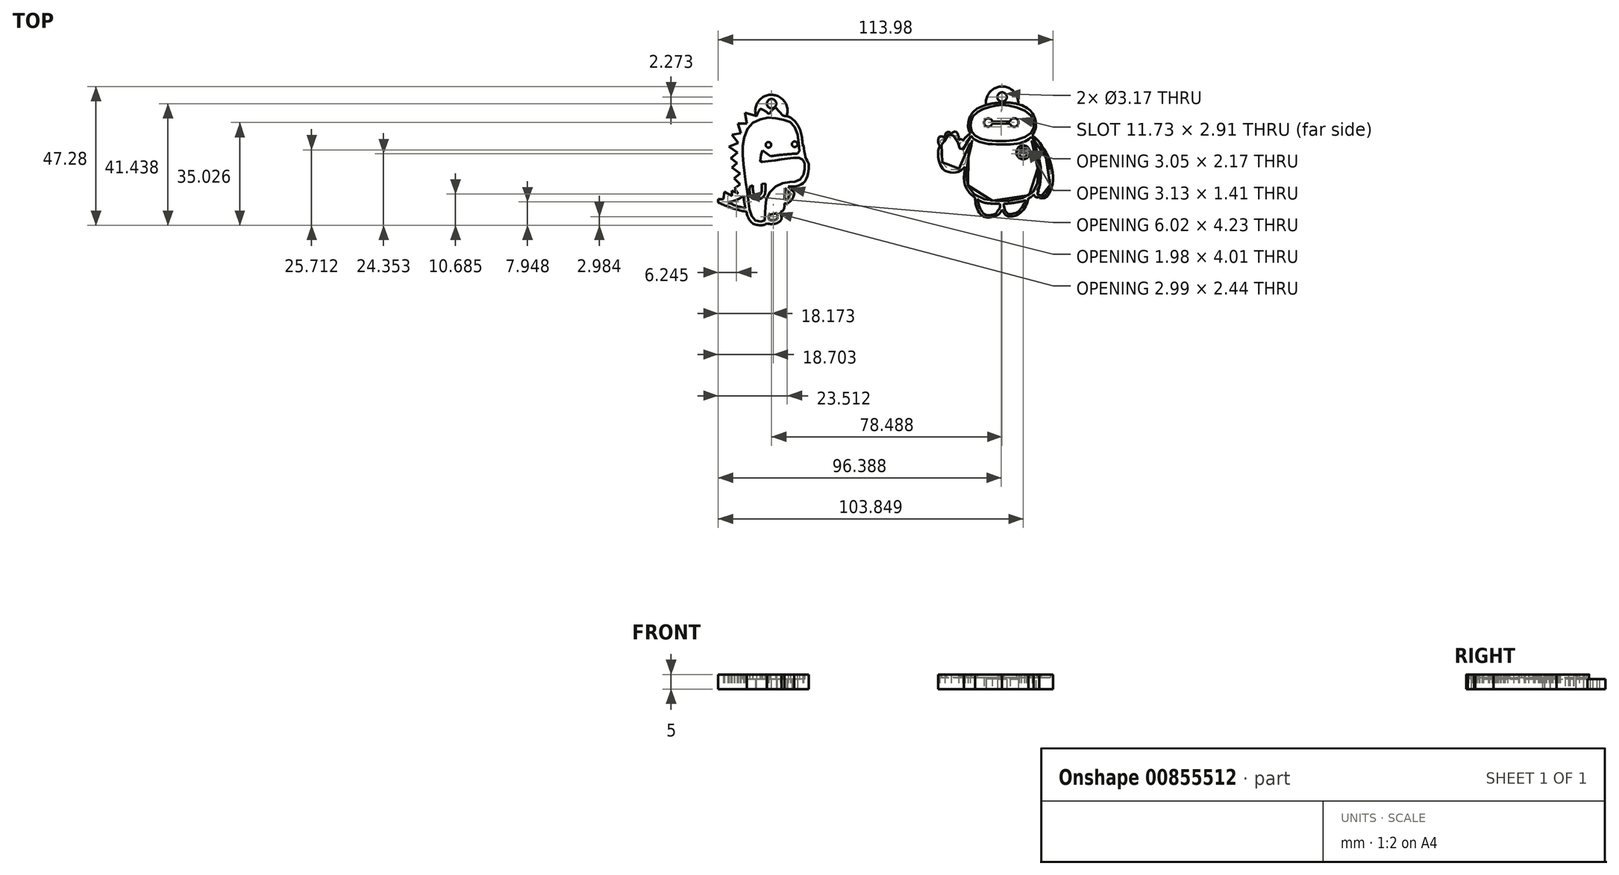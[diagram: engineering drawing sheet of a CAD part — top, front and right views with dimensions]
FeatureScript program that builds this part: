
annotation { "Feature Type Name" : "Feature", "Feature Type Description" : "" }
export const myFeature = defineFeature(function(context is Context, id is Id, definition is map)
    precondition{}
    {
        {
            var Q0;
            Q0=qCreatedBy(makeId("Top.planeOp"),FACE);
            var sketch = newSketch(context, id + "F0", { "sketchPlane" : qUnion([Q0])});
            skFitSpline(sketch, "E0", {"points": [v(-13.55, 2.38) * mm, v(-14.14, 6.7) * mm, v(-15.54, 10.04) * mm, v(-18.18, 12.36) * mm, v(-20.34, 12.79) * mm], "startDerivative": vector(-1.53, 15.7) * mm, "endDerivative": vector(-10.5, 0.69) * mm});
            skLineSegment(sketch, "E1", {"start": v(-20.34, 12.79) * mm, "end": v(-22.82, 15.65) * mm});
            skFitSpline(sketch, "E2", {"points": [v(-22.82, 15.65) * mm, v(-24.28, 14.43) * mm, v(-25.04, 13.33) * mm], "startDerivative": vector(-2.96, -2.18) * mm, "endDerivative": vector(-1.42, -2.46) * mm});
            skFitSpline(sketch, "E3", {"points": [v(-25.04, 13.33) * mm, v(-26.95, 14.76) * mm, v(-28.08, 15.13) * mm], "startDerivative": vector(-3.43, 2.89) * mm, "endDerivative": vector(-2.63, 0.6) * mm});
            skFitSpline(sketch, "E4", {"points": [v(-28.08, 15.13) * mm, v(-28.76, 14) * mm, v(-29.3, 12.68) * mm], "startDerivative": vector(-1.45, -2.24) * mm, "endDerivative": vector(-0.98, -2.66) * mm});
            skFitSpline(sketch, "E5", {"points": [v(-29.3, 12.68) * mm, v(-33.32, 13.87) * mm], "startDerivative": vector(-4.02, 1.19) * mm, "endDerivative": vector(-4.02, 1.19) * mm});
            skLineSegment(sketch, "E6", {"start": v(-33.32, 13.87) * mm, "end": v(-32.7, 10.17) * mm});
            skLineSegment(sketch, "E7", {"start": v(-32.7, 10.17) * mm, "end": v(-35.72, 10.17) * mm});
            skLineSegment(sketch, "E8", {"start": v(-35.72, 10.17) * mm, "end": v(-34.67, 6.85) * mm});
            skLineSegment(sketch, "E9", {"start": v(-34.67, 6.85) * mm, "end": v(-37.66, 6.31) * mm});
            skLineSegment(sketch, "E10", {"start": v(-37.66, 6.31) * mm, "end": v(-35.58, 3.6) * mm});
            skLineSegment(sketch, "E11", {"start": v(-35.58, 3.6) * mm, "end": v(-38.74, 2.24) * mm});
            skLineSegment(sketch, "E12", {"start": v(-38.74, 2.24) * mm, "end": v(-35.82, 0.22) * mm});
            skLineSegment(sketch, "E13", {"start": v(-35.82, 0.22) * mm, "end": v(-38.06, -1.67) * mm});
            skLineSegment(sketch, "E14", {"start": v(-38.06, -1.67) * mm, "end": v(-35.88, -3.34) * mm});
            skLineSegment(sketch, "E15", {"start": v(-35.88, -3.34) * mm, "end": v(-37.71, -4.85) * mm});
            skLineSegment(sketch, "E16", {"start": v(-37.71, -4.85) * mm, "end": v(-34.93, -6.82) * mm});
            skLineSegment(sketch, "E17", {"start": v(-34.93, -6.82) * mm, "end": v(-36.98, -8.5) * mm});
            skLineSegment(sketch, "E18", {"start": v(-36.98, -8.5) * mm, "end": v(-34.93, -10.49) * mm});
            skLineSegment(sketch, "E19", {"start": v(-34.93, -10.49) * mm, "end": v(-36.85, -11.95) * mm});
            skLineSegment(sketch, "E20", {"start": v(-36.85, -11.95) * mm, "end": v(-35.53, -13.68) * mm});
            skLineSegment(sketch, "E21", {"start": v(-35.53, -13.68) * mm, "end": v(-37.66, -12.76) * mm});
            skLineSegment(sketch, "E22", {"start": v(-37.66, -12.76) * mm, "end": v(-37.66, -14.54) * mm});
            skLineSegment(sketch, "E23", {"start": v(-37.66, -14.54) * mm, "end": v(-40.22, -13.08) * mm});
            skLineSegment(sketch, "E24", {"start": v(-40.22, -13.08) * mm, "end": v(-40.68, -15.61) * mm});
            skLineSegment(sketch, "E25", {"start": v(-40.68, -15.61) * mm, "end": v(-42.38, -15.61) * mm});
            skLineSegment(sketch, "E26", {"start": v(-42.38, -15.61) * mm, "end": v(-42.38, -16.75) * mm});
            skFitSpline(sketch, "E27", {"points": [v(-42.38, -16.75) * mm, v(-38.06, -18.5) * mm, v(-32.7, -19.98) * mm], "startDerivative": vector(8.74, -3.87) * mm, "endDerivative": vector(10.6, -2.62) * mm});
            skFitSpline(sketch, "E28", {"points": [v(-33.13, -18.69) * mm, v(-33.59, -16.23) * mm, v(-33.77, -14.45) * mm], "startDerivative": vector(-0.96, 4.7) * mm, "endDerivative": vector(-0.31, 3.73) * mm});
            skFitSpline(sketch, "E29", {"points": [v(-33.77, -14.45) * mm, v(-35.9, -15.78) * mm, v(-39.14, -16.75) * mm], "startDerivative": vector(-4.28, -3.1) * mm, "endDerivative": vector(-6.4, -1.53) * mm});
            skFitSpline(sketch, "E30", {"points": [v(-39.14, -16.75) * mm, v(-36.74, -17.7) * mm, v(-34.53, -18.4) * mm, v(-33.13, -18.69) * mm], "startDerivative": vector(6.42, -2.62) * mm, "endDerivative": vector(4.8, -0.89) * mm});
            skCircle(sketch, "E31", {"center": v(-25.27, 2.88) * mm, "radius": 0.94 * mm});
            skCircle(sketch, "E32", {"center": v(-16.34, 3.1) * mm, "radius": 0.94 * mm});
            skFitSpline(sketch, "E33", {"points": [v(-32.7, -19.98) * mm, v(-32.33, -21.5) * mm, v(-30.9, -23.65) * mm, v(-29.2, -24.4) * mm, v(-26.91, -24.42) * mm, v(-25.82, -23.82) * mm], "startDerivative": vector(1.1, -7.8) * mm, "endDerivative": vector(5.74, 4.5) * mm});
            skFitSpline(sketch, "E34", {"points": [v(-25.82, -23.82) * mm, v(-24.76, -24.07) * mm, v(-22.61, -23.82) * mm, v(-20.95, -22.56) * mm, v(-21.24, -19.98) * mm], "startDerivative": vector(5.1, -1.72) * mm, "endDerivative": vector(-2.9, 9.83) * mm});
            skFitSpline(sketch, "E35", {"points": [v(-21.24, -19.98) * mm, v(-20.27, -19.45) * mm, v(-19.86, -18.2) * mm, v(-19.86, -17.01) * mm], "startDerivative": vector(3.4, 1.17) * mm, "endDerivative": vector(-0.19, 3.45) * mm});
            skFitSpline(sketch, "E36", {"points": [v(-19.86, -17.01) * mm, v(-18.73, -17.01) * mm, v(-17.07, -15.35) * mm, v(-16.58, -13.4) * mm, v(-17.29, -12.59) * mm, v(-18.5, -11.3) * mm], "startDerivative": vector(6.54, -1.35) * mm, "endDerivative": vector(-5.93, 6.76) * mm});
            skFitSpline(sketch, "E37", {"points": [v(-18.5, -11.3) * mm, v(-16.3, -11.3) * mm, v(-13.28, -10) * mm, v(-11.7, -6.53) * mm, v(-11.64, -3.38) * mm, v(-12.48, -1.75) * mm, v(-13.28, 2.78) * mm], "startDerivative": vector(14.75, -1.2) * mm, "endDerivative": vector(-2.71, 25.65) * mm});
            skFitSpline(sketch, "E38", {"points": [v(-13.28, 2.78) * mm, v(-13.55, 2.38) * mm], "startDerivative": vector(-0.26, -0.4) * mm, "endDerivative": vector(-0.26, -0.4) * mm});
            skFitSpline(sketch, "E39", {"points": [v(-31.58, -11.3) * mm, v(-30.59, -10.94) * mm], "startDerivative": vector(1, 0.36) * mm, "endDerivative": vector(1, 0.36) * mm});
            skFitSpline(sketch, "E40", {"points": [v(-31.58, -11.3) * mm, v(-31.71, -12.51) * mm, v(-31.34, -14.6) * mm, v(-30.3, -15.56) * mm, v(-28.36, -15.62) * mm, v(-26.77, -14.5) * mm, v(-26.37, -13.31) * mm, v(-26.32, -10.27) * mm], "startDerivative": vector(-1.66, -9.24) * mm, "endDerivative": vector(-0.24, 18.42) * mm});
            skFitSpline(sketch, "E41", {"points": [v(-30.59, -10.94) * mm, v(-30.59, -12.35) * mm, v(-30.19, -13.84) * mm, v(-29.28, -14.6) * mm, v(-28.04, -13.99) * mm, v(-27.54, -12.82) * mm, v(-27.56, -10.38) * mm], "startDerivative": vector(-0.38, -8.61) * mm, "endDerivative": vector(-0.72, 12.58) * mm});
            skFitSpline(sketch, "E42", {"points": [v(-27.56, -10.38) * mm, v(-26.32, -10.27) * mm], "startDerivative": vector(1.23, 0.11) * mm, "endDerivative": vector(1.23, 0.11) * mm});
            skFitSpline(sketch, "E43", {"points": [v(-25.17, -20.9) * mm, v(-23.34, -20.61) * mm, v(-22.45, -20.31) * mm], "startDerivative": vector(3.43, 0.45) * mm, "endDerivative": vector(1.94, 0.76) * mm});
            skFitSpline(sketch, "E44", {"points": [v(-25.17, -20.9) * mm, v(-25.17, -22.49) * mm], "startDerivative": vector(0, -1.58) * mm, "endDerivative": vector(0, -1.58) * mm});
            skFitSpline(sketch, "E45", {"points": [v(-25.17, -22.49) * mm, v(-24.72, -22.7) * mm, v(-23.5, -22.73) * mm, v(-22.52, -22.49) * mm, v(-22.2, -22.03) * mm, v(-22.22, -21.27) * mm, v(-22.45, -20.31) * mm], "startDerivative": vector(2.97, -1.91) * mm, "endDerivative": vector(-1.45, 5.3) * mm});
            skFitSpline(sketch, "E46", {"points": [v(-19.86, -15.84) * mm, v(-19.67, -11.83) * mm], "startDerivative": vector(0.18, 4) * mm, "endDerivative": vector(0.18, 4) * mm});
            skFitSpline(sketch, "E47", {"points": [v(-19.67, -11.83) * mm, v(-18.7, -12.96) * mm, v(-17.9, -13.67) * mm, v(-17.88, -14.04) * mm, v(-18.23, -14.7) * mm, v(-19.04, -15.6) * mm, v(-19.86, -15.84) * mm], "startDerivative": vector(4.22, -5.71) * mm, "endDerivative": vector(-5.2, -0.73) * mm});
            skFitSpline(sketch, "E48", {"points": [v(-24.55, -1.02) * mm, v(-20.5, -0.46) * mm, v(-17.07, -0.18) * mm, v(-15.46, -0.14) * mm], "startDerivative": vector(10.3, 1.59) * mm, "endDerivative": vector(5.92, 0.1) * mm});
            skFitSpline(sketch, "E49", {"points": [v(-15.46, -0.14) * mm, v(-14.75, 0.77) * mm], "startDerivative": vector(0.7, 0.9) * mm, "endDerivative": vector(0.7, 0.9) * mm});
            skFitSpline(sketch, "E50", {"points": [v(-14.75, 0.77) * mm, v(-15.12, 5.03) * mm, v(-16.34, 8.98) * mm, v(-18.04, 10.7) * mm, v(-21.24, 11.68) * mm, v(-24.7, 12.15) * mm, v(-28.7, 11.36) * mm, v(-31.76, 9.32) * mm, v(-33.71, 4.9) * mm, v(-34.05, 0.3) * mm, v(-33.62, -5) * mm, v(-33.01, -9.96) * mm, v(-32.29, -14.9) * mm, v(-31.58, -19.67) * mm, v(-30.59, -22.07) * mm, v(-29.04, -23.07) * mm, v(-27.56, -23.18) * mm, v(-26.52, -22.91) * mm], "startDerivative": vector(-2.74, 64.84) * mm, "endDerivative": vector(30.23, 10.18) * mm});
            skFitSpline(sketch, "E51", {"points": [v(-26.52, -22.91) * mm, v(-26.32, -18.87) * mm, v(-25.82, -15) * mm, v(-22.28, -10.94) * mm, v(-18.1, -9.76) * mm, v(-15.75, -9.6) * mm, v(-13.55, -7.8) * mm, v(-13, -5.47) * mm, v(-12.98, -3.04) * mm, v(-13.85, -2.02) * mm, v(-15.25, -1.5) * mm, v(-17.95, -1.64) * mm, v(-20.91, -2.06) * mm, v(-24.37, -2.54) * mm, v(-27.56, -3) * mm, v(-27.98, -3) * mm, v(-27.93, -0.91) * mm, v(-27.25, 0.97) * mm], "startDerivative": vector(3.63, 55.97) * mm, "endDerivative": vector(15.3, 32.1) * mm});
            skFitSpline(sketch, "E52", {"points": [v(-27.25, 0.97) * mm, v(-24.55, -1.02) * mm], "startDerivative": vector(2.7, -2) * mm, "endDerivative": vector(2.7, -2) * mm});
            skArc(sketch, "E53", {"start": v(-19.08, 12.65) * mm, "mid": v(-24.23, 19.93) * mm, "end": v(-29.51, 12.74) * mm});
            skCircle(sketch, "E54", {"center": v(-24.2, 16.92) * mm, "radius": 1.59 * mm});
            skFitSpline(sketch, "E55", {"points": [v(52.83, 17.2) * mm, v(57.19, 17.2) * mm, v(61.36, 16.2) * mm, v(64.4, 13.95) * mm, v(65.79, 10.46) * mm, v(65.6, 7.99) * mm, v(64.57, 6.22) * mm], "startDerivative": vector(23.07, 1.03) * mm, "endDerivative": vector(-9.18, -12.95) * mm});
            skFitSpline(sketch, "E56", {"points": [v(52.83, 17.2) * mm, v(49.94, 16.77) * mm, v(46.6, 15.62) * mm, v(44.62, 14.27) * mm, v(43.27, 12.22) * mm, v(42.75, 10.3) * mm, v(42.85, 8.15) * mm, v(43.46, 6.73) * mm], "startDerivative": vector(-17.72, -1.72) * mm, "endDerivative": vector(6.22, -11.36) * mm});
            skFitSpline(sketch, "E57", {"points": [v(43.46, 6.73) * mm, v(42.45, 5.98) * mm, v(41.47, 4.99) * mm, v(40.94, 4.32) * mm], "startDerivative": vector(-2.92, -1.98) * mm, "endDerivative": vector(-1.67, -2.23) * mm});
            skFitSpline(sketch, "E58", {"points": [v(40.94, 4.32) * mm, v(40.6, 4.68) * mm, v(40.07, 4.83) * mm, v(39.5, 4.57) * mm], "startDerivative": vector(-0.93, 1.29) * mm, "endDerivative": vector(-1.6, -1) * mm});
            skFitSpline(sketch, "E59", {"points": [v(39.5, 4.57) * mm, v(39.5, 5.44) * mm, v(39.2, 6.45) * mm, v(38.7, 7.3) * mm, v(38, 7.4) * mm, v(37.31, 6.96) * mm, v(37.01, 6.2) * mm], "startDerivative": vector(0.38, 5.14) * mm, "endDerivative": vector(-1.3, -5.03) * mm});
            skFitSpline(sketch, "E60", {"points": [v(37.01, 6.2) * mm, v(36.58, 7.04) * mm, v(36, 7.3) * mm, v(35.47, 7.14) * mm, v(35.09, 6.73) * mm, v(34.86, 6.2) * mm, v(34.8, 5.52) * mm, v(34.85, 4.86) * mm], "startDerivative": vector(-2.07, 5.55) * mm, "endDerivative": vector(0.47, -4.5) * mm});
            skFitSpline(sketch, "E61", {"points": [v(34.85, 4.86) * mm, v(34.36, 5.44) * mm, v(33.79, 5.77) * mm, v(33.02, 5.63) * mm, v(32.63, 5.09) * mm, v(32.52, 3.64) * mm, v(32.82, 2.94) * mm, v(33.06, 2.47) * mm], "startDerivative": vector(-3.3, 4.35) * mm, "endDerivative": vector(1.91, -3.92) * mm});
            skFitSpline(sketch, "E62", {"points": [v(33.06, 2.47) * mm, v(32.7, 1.48) * mm, v(32.49, -0.2) * mm, v(32.6, -1.84) * mm, v(33.06, -3.5) * mm, v(34, -5.18) * mm, v(35.13, -6.03) * mm, v(38.16, -6.57) * mm, v(40.09, -5.87) * mm, v(41.66, -4.54) * mm], "startDerivative": vector(-4.76, -10.76) * mm, "endDerivative": vector(12.96, 12.08) * mm});
            skFitSpline(sketch, "E63", {"points": [v(41.66, -4.54) * mm, v(41.47, -6.27) * mm, v(41.36, -9.32) * mm, v(41.98, -11.6) * mm, v(43.46, -13.74) * mm, v(45.06, -15.14) * mm], "startDerivative": vector(-1.09, -9.17) * mm, "endDerivative": vector(8.58, -6.65) * mm});
            skFitSpline(sketch, "E64", {"points": [v(45.06, -15.14) * mm, v(45.23, -16.76) * mm, v(45.82, -18.9) * mm, v(47.05, -20.9) * mm, v(48.74, -21.78) * mm, v(50.98, -21.71) * mm, v(52.94, -20.96) * mm, v(53.6, -20.27) * mm, v(54.22, -19.25) * mm], "startDerivative": vector(0.88, -13.14) * mm, "endDerivative": vector(6.2, 10.64) * mm});
            skFitSpline(sketch, "E65", {"points": [v(54.22, -19.25) * mm, v(54.8, -20.2) * mm, v(56.02, -21.36) * mm, v(57.66, -21.47) * mm, v(59.64, -20.9) * mm, v(61.68, -19) * mm, v(62.87, -16.73) * mm, v(63.32, -15.36) * mm], "startDerivative": vector(4.53, -8.12) * mm, "endDerivative": vector(3.02, 10.17) * mm});
            skFitSpline(sketch, "E66", {"points": [v(63.32, -15.36) * mm, v(64.7, -14.45) * mm, v(65.06, -13.97) * mm], "startDerivative": vector(2.6, 1.53) * mm, "endDerivative": vector(0.75, 1.24) * mm});
            skFitSpline(sketch, "E67", {"points": [v(65.06, -13.97) * mm, v(65.3, -14.38) * mm, v(65.65, -14.8) * mm, v(66.42, -15.03) * mm, v(66.91, -14.8) * mm], "startDerivative": vector(1.04, -1.82) * mm, "endDerivative": vector(1.83, 1.3) * mm});
            skFitSpline(sketch, "E68", {"points": [v(66.91, -14.8) * mm, v(67.03, -15.14) * mm, v(67.96, -15.36) * mm, v(69.37, -14.88) * mm, v(70.68, -12.86) * mm, v(71.46, -10.29) * mm, v(71.55, -7.08) * mm, v(71.02, -4.08) * mm, v(69.81, -0.8) * mm, v(67.82, 2.66) * mm, v(66.44, 4.42) * mm, v(64.92, 5.87) * mm, v(64.57, 6.22) * mm], "startDerivative": vector(0.82, -10.48) * mm, "endDerivative": vector(-6.71, 7.06) * mm});
            skCircle(sketch, "E69", {"center": v(49.56, 10.48) * mm, "radius": 1.42 * mm});
            skCircle(sketch, "E70", {"center": v(58.41, 10.5) * mm, "radius": 1.46 * mm});
            skLineSegment(sketch, "E71", {"start": v(50.95, 10.78) * mm, "end": v(56.98, 10.78) * mm});
            skLineSegment(sketch, "E72", {"start": v(50.96, 10.21) * mm, "end": v(56.98, 10.21) * mm});
            skArc(sketch, "E73", {"start": v(59.76, 16.74) * mm, "mid": v(54.15, 22.75) * mm, "end": v(48.84, 16.48) * mm});
            skCircle(sketch, "E74", {"center": v(54.28, 19.2) * mm, "radius": 1.59 * mm});
            skFitSpline(sketch, "E75", {"points": [v(54.35, 16.46) * mm, v(51.09, 16.02) * mm, v(48.36, 15.3) * mm, v(45.79, 13.88) * mm, v(43.95, 11.92) * mm, v(43.54, 10.12) * mm, v(43.67, 8.08) * mm, v(44.89, 6.21) * mm, v(47.4, 4.9) * mm, v(51.24, 4.29) * mm, v(58.35, 4.46) * mm, v(63.5, 6.38) * mm, v(64.93, 8.6) * mm, v(64.84, 11.3) * mm, v(62.9, 14.05) * mm, v(57.82, 15.98) * mm, v(54.35, 16.46) * mm]});
            skFitSpline(sketch, "E76", {"points": [v(43.7, 6.02) * mm, v(42.39, 4.76) * mm, v(41.32, 3.27) * mm, v(40.77, 2.42) * mm, v(40.88, 1.58) * mm, v(41.2, 0.55) * mm, v(41.2, -0.33) * mm, v(40.79, -0.44) * mm, v(40.3, -0.14) * mm, v(40.2, 0.93) * mm, v(39.8, 1.86) * mm, v(39.74, 2.51) * mm, v(40.31, 3.35) * mm, v(40.5, 3.88) * mm, v(40.06, 4.06) * mm, v(39.78, 4.04) * mm, v(39.28, 3.73) * mm, v(39, 3.83) * mm, v(38.88, 4.82) * mm, v(38.69, 5.93) * mm, v(38.38, 6.57) * mm, v(38.06, 6.57) * mm, v(37.75, 6.02) * mm, v(37.56, 5.05) * mm, v(37.26, 4.82) * mm, v(36.82, 4.78) * mm, v(36.57, 5.07) * mm, v(36.48, 5.9) * mm, v(36.25, 6.35) * mm, v(35.94, 6.46) * mm, v(35.4, 6.04) * mm, v(35.4, 5.18) * mm, v(35.4, 4.29) * mm, v(35.27, 3.92) * mm, v(34.63, 3.62) * mm, v(34.53, 4.2) * mm, v(34.15, 4.69) * mm, v(33.83, 4.9) * mm, v(33.31, 4.6) * mm, v(33.18, 4.32) * mm, v(33.14, 3.77) * mm, v(33.46, 3.14) * mm, v(33.75, 2.5) * mm, v(33.62, 1.75) * mm, v(33.23, 0.15) * mm, v(33.52, -2.05) * mm, v(34.38, -4.07) * mm, v(35.75, -5.35) * mm, v(37.41, -5.67) * mm, v(39.76, -5.16) * mm, v(41.63, -3.5) * mm, v(42.2, -1.3) * mm, v(43.84, 4.46) * mm, v(44.07, 4.42) * mm, v(44.07, 3.98) * mm, v(43.86, 2.97) * mm, v(42.71, -1.7) * mm, v(42.2, -6.41) * mm, v(42.43, -9.85) * mm, v(43.97, -13.22) * mm, v(47.88, -15.5) * mm, v(52.92, -16.18) * mm, v(60.5, -15.44) * mm, v(65.1, -12.77) * mm, v(66.42, -9.2) * mm, v(66.42, -4.45) * mm, v(65.5, 0.03) * mm, v(64.55, 3.31) * mm, v(64.38, 4.4) * mm, v(64.57, 4.38) * mm, v(64.91, 4.1) * mm, v(65.9, 1.65) * mm, v(67.05, -2.28) * mm, v(67.47, -6.1) * mm, v(67.34, -9.64) * mm, v(66.92, -11.4) * mm, v(66.2, -12.73) * mm, v(66.38, -12.7) * mm, v(66.82, -12.8) * mm, v(66.9, -13.17) * mm, v(66.61, -13.43) * mm, v(66.3, -13.83) * mm, v(66.17, -14.25) * mm, v(66.61, -14.27) * mm, v(66.82, -13.97) * mm, v(67.07, -13.72) * mm, v(67.58, -13.7) * mm, v(67.68, -13.9) * mm, v(67.58, -14.3) * mm, v(67.7, -14.54) * mm, v(67.97, -14.6) * mm, v(68.63, -14.58) * mm, v(69.17, -13.97) * mm, v(69.38, -13.74) * mm, v(70.31, -11.77) * mm, v(70.9, -8.7) * mm, v(70.64, -5.58) * mm, v(68.65, -0.3) * mm, v(66.06, 3.75) * mm, v(64.76, 4.97) * mm, v(64.2, 5.53) * mm], "startDerivative": vector(-114.33, -97.1) * mm, "endDerivative": vector(-63.13, 67.13) * mm});
            skFitSpline(sketch, "E77", {"points": [v(43.7, 6.02) * mm, v(44.75, 4.86) * mm, v(47.98, 3.48) * mm, v(54.73, 3) * mm, v(60.03, 3.39) * mm, v(63.06, 4.63) * mm, v(64.2, 5.53) * mm], "startDerivative": vector(7.66, -10.47) * mm, "endDerivative": vector(9.04, 8.09) * mm});
            skFitSpline(sketch, "E78", {"points": [v(45.89, -15.66) * mm, v(47.61, -16.61) * mm, v(51.44, -17.18) * mm, v(53.52, -17.18) * mm], "startDerivative": vector(4.97, -3.6) * mm, "endDerivative": vector(6.14, 0.2) * mm});
            skFitSpline(sketch, "E79", {"points": [v(53.52, -17.18) * mm, v(53.52, -18.37) * mm, v(52.9, -19.47) * mm, v(52.06, -20.52) * mm, v(50.2, -21.04) * mm, v(48.48, -20.88) * mm, v(47.45, -19.8) * mm, v(46.5, -17.99) * mm, v(45.89, -15.66) * mm], "startDerivative": vector(1.47, -11.52) * mm, "endDerivative": vector(-3.42, 15.92) * mm});
            skFitSpline(sketch, "E80", {"points": [v(54.9, -17.18) * mm, v(58.19, -16.88) * mm, v(62.5, -16.01) * mm], "startDerivative": vector(6.87, 0.4) * mm, "endDerivative": vector(8.31, 1.9) * mm});
            skFitSpline(sketch, "E81", {"points": [v(62.5, -16.01) * mm, v(61.8, -17.18) * mm, v(60.48, -19.15) * mm, v(59.16, -20.2) * mm, v(57.38, -20.66) * mm, v(56.06, -20.44) * mm, v(55.22, -19.2) * mm, v(54.92, -17.9) * mm, v(54.9, -17.18) * mm], "startDerivative": vector(-5.32, -8.88) * mm, "endDerivative": vector(0.01, 7.76) * mm});
            skCircle(sketch, "E82", {"center": v(61.47, 0.32) * mm, "radius": 2.34 * mm});
            skCircle(sketch, "E83", {"center": v(61.47, 0.32) * mm, "radius": 1.57 * mm});
            skLineSegment(sketch, "E84", {"start": v(59.9, 0.49) * mm, "end": v(60.22, 0.49) * mm});
            skFitSpline(sketch, "E85", {"points": [v(60.22, 0.49) * mm, v(60.34, 0.92) * mm, v(60.7, 1.27) * mm, v(61.39, 1.41) * mm, v(62, 1.36) * mm, v(62.37, 1.04) * mm, v(62.51, 0.49) * mm], "startDerivative": vector(0.52, 2.95) * mm, "endDerivative": vector(0.48, -3.52) * mm});
            skLineSegment(sketch, "E86", {"start": v(62.51, 0.49) * mm, "end": v(63.03, 0.49) * mm});
            skLineSegment(sketch, "E87", {"start": v(59.94, -0.06) * mm, "end": v(60.82, -0.06) * mm});
            skFitSpline(sketch, "E88", {"points": [v(60.82, -0.06) * mm, v(60.82, 0.4) * mm, v(61.01, 0.78) * mm, v(61.48, 0.92) * mm, v(61.8, 0.79) * mm, v(61.9, 0.55) * mm, v(61.9, 0.16) * mm, v(61.92, -0.06) * mm], "startDerivative": vector(-0.22, 2.88) * mm, "endDerivative": vector(0.08, -1.83) * mm});
            skLineSegment(sketch, "E89", {"start": v(61.92, -0.06) * mm, "end": v(63, -0.06) * mm});
            skSolve(sketch);
        }
        {
            var Q0;
            {var subQ0=sQuery(id+"F0.wireOp",EDGE,"E1");Q0=makeQuery(id+"F0.imprint","IMPRINT",FACE,{"disambiguationData":[TD([[makeQuery(id+"F0.imprint","IMPRINT",EDGE,{"derivedFrom":subQ0}),-1.0]])]});}
            var Q1;
            Q1=makeQuery(id+"F0.imprint","IMPRINT",FACE,{"disambiguationData":[TD([[makeQuery(id+"F0.imprint","IMPRINT",EDGE,{"derivedFrom":sQuery(id+"F0.wireOp",EDGE,"E31")}),-1.0]])]});
            extrude(context, id + "F1", {"entities" : qUnion([Q0, Q1]), "depth" : 3.5 * mm, "offsetDistance" : 25 * mm});
        }
        {
            var Q0;
            {var subQ8=sQuery(id+"F0.wireOp",EDGE,"E1");Q0=makeQuery(id+"F0.imprint","IMPRINT",FACE,{"disambiguationData":[TD([[makeQuery(id+"F0.imprint","IMPRINT",EDGE,{"derivedFrom":subQ8}),1.0]])]});}
            var Q1;
            Q1=makeQuery(id+"F0.imprint","IMPRINT",FACE,{"disambiguationData":[TD([[makeQuery(id+"F0.imprint","IMPRINT",EDGE,{"derivedFrom":sQuery(id+"F0.wireOp",EDGE,"E39")}),-1.0]])]});
            extrude(context, id + "F2", {"entities" : qUnion([Q0, Q1]), "operationType" : NewBodyOperationType.ADD, "depth" : 5 * mm, "offsetDistance" : 25 * mm});
        }
        {
            var Q0;
            {var subQ3=sQuery(id+"F0.wireOp",EDGE,"E73");Q0=makeQuery(id+"F0.imprint","IMPRINT",FACE,{"disambiguationData":[TD([[makeQuery(id+"F0.imprint","IMPRINT",EDGE,{"derivedFrom":subQ3}),1.0]])]});}
            extrude(context, id + "F3", {"entities" : qUnion([Q0]), "depth" : 3.5 * mm, "offsetDistance" : 25 * mm});
        }
        {
            var Q0;
            {var subQ1=sQuery(id+"F0.wireOp",EDGE,"E57");Q0=makeQuery(id+"F0.imprint","IMPRINT",FACE,{"disambiguationData":[TD([[makeQuery(id+"F0.imprint","IMPRINT",EDGE,{"derivedFrom":subQ1}),1.0]])]});}
            extrude(context, id + "F4", {"entities" : qUnion([Q0]), "operationType" : NewBodyOperationType.ADD, "depth" : 5 * mm, "offsetDistance" : 25 * mm});
        }
        {
            var Q0;
            {var subQ0=sQuery(id+"F0.wireOp",EDGE,"E71");Q0=makeQuery(id+"F0.imprint","IMPRINT",FACE,{"disambiguationData":[TD([[makeQuery(id+"F0.imprint","IMPRINT",EDGE,{"derivedFrom":subQ0}),1.0]])]});}
            var Q1;
            Q1=makeQuery(id+"F0.imprint","IMPRINT",FACE,{"disambiguationData":[TD([[makeQuery(id+"F0.imprint","IMPRINT",EDGE,{"derivedFrom":sQuery(id+"F0.wireOp",EDGE,"E76")}),1.0]])]});
            var Q2;
            Q2=makeQuery(id+"F0.imprint","IMPRINT",FACE,{"disambiguationData":[TD([[makeQuery(id+"F0.imprint","IMPRINT",EDGE,{"derivedFrom":sQuery(id+"F0.wireOp",EDGE,"E78")}),-1.0]])]});
            var Q3;
            Q3=makeQuery(id+"F0.imprint","IMPRINT",FACE,{"disambiguationData":[TD([[makeQuery(id+"F0.imprint","IMPRINT",EDGE,{"derivedFrom":sQuery(id+"F0.wireOp",EDGE,"E80")}),-1.0]])]});
            extrude(context, id + "F5", {"entities" : qUnion([Q0, Q1, Q2, Q3]), "operationType" : NewBodyOperationType.ADD, "depth" : 4 * mm, "offsetDistance" : 25 * mm});
        }
        {
            var Q0;
            Q0=makeQuery(id+"F0.imprint","IMPRINT",FACE,{"disambiguationData":[TD([[makeQuery(id+"F0.imprint","IMPRINT",EDGE,{"derivedFrom":sQuery(id+"F0.wireOp",EDGE,"E82")}),1.0]])]});
            var Q1;
            {var subQ0=sQuery(id+"F0.wireOp",EDGE,"E84");Q1=makeQuery(id+"F0.imprint","IMPRINT",FACE,{"disambiguationData":[TD([[makeQuery(id+"F0.imprint","IMPRINT",EDGE,{"derivedFrom":subQ0}),-1.0]])]});}
            extrude(context, id + "F6", {"entities" : qUnion([Q0, Q1]), "operationType" : NewBodyOperationType.ADD, "depth" : 5 * mm, "offsetDistance" : 25 * mm});
        }
    });
